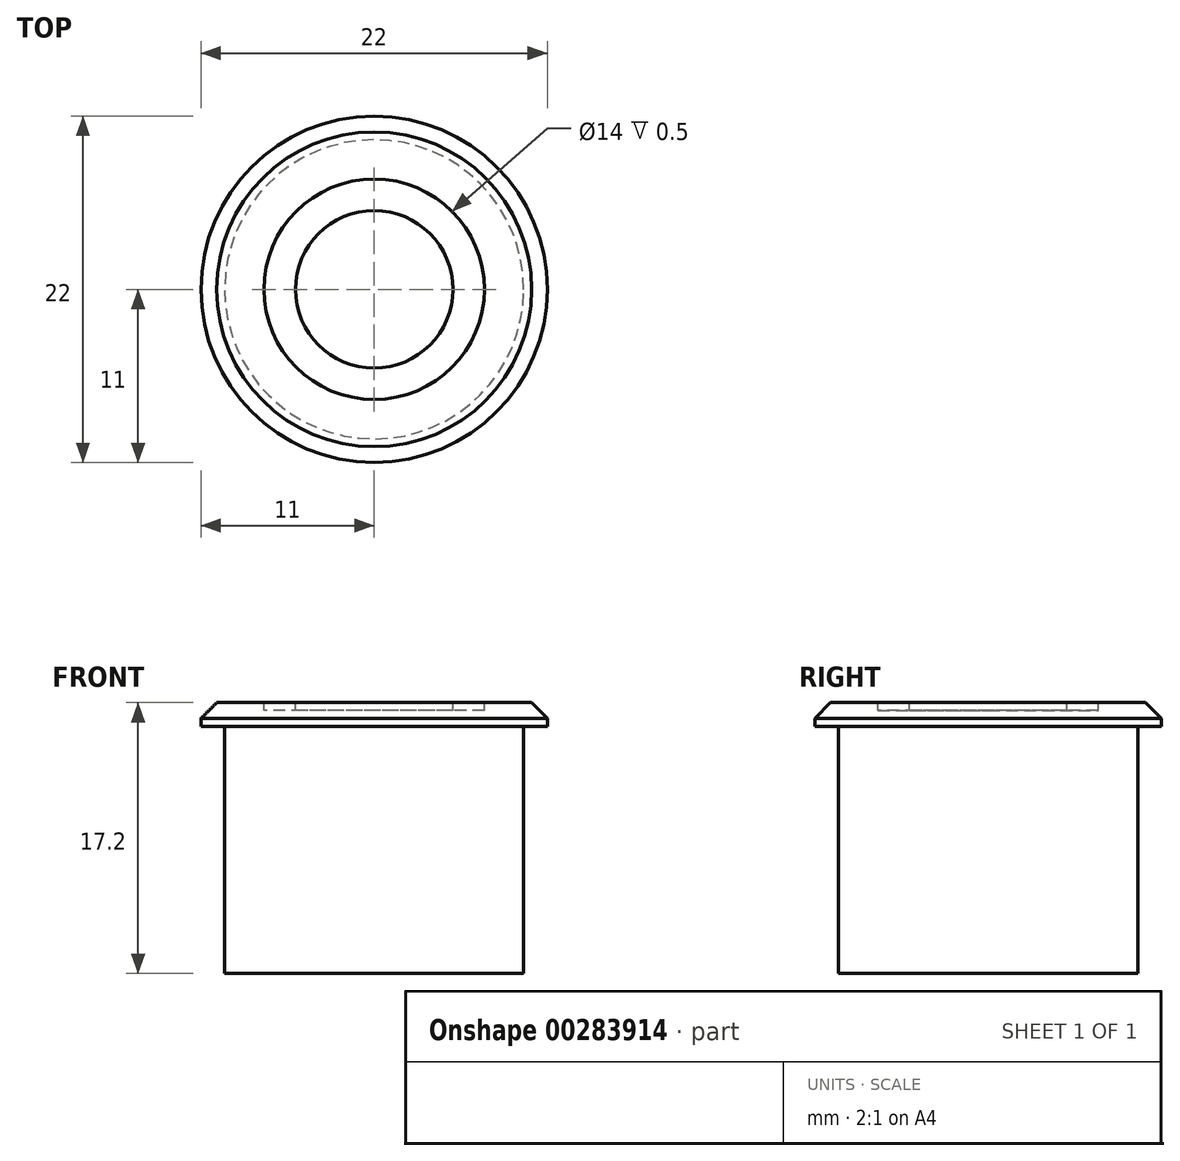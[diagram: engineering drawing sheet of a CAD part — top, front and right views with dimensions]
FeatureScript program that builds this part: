
annotation { "Feature Type Name" : "Feature", "Feature Type Description" : "" }
export const myFeature = defineFeature(function(context is Context, id is Id, definition is map)
    precondition{}
    {
        {
            var Q0;
            Q0=qCreatedBy(makeId("Right.planeOp"),FACE);
            var sketch = newSketch(context, id + "F0", { "sketchPlane" : qUnion([Q0])});
            skLineSegment(sketch, "E0", {"start": v(0, 0) * mm, "end": v(0, 17.2) * mm});
            skLineSegment(sketch, "E1", {"start": v(0, 17.2) * mm, "end": v(10, 17.2) * mm});
            skLineSegment(sketch, "E2", {"start": v(10, 17.2) * mm, "end": v(11, 16.2) * mm});
            skLineSegment(sketch, "E3", {"start": v(11, 16.2) * mm, "end": v(11, 15.7) * mm});
            skLineSegment(sketch, "E4", {"start": v(11, 15.7) * mm, "end": v(9.5, 15.7) * mm});
            skLineSegment(sketch, "E5", {"start": v(9.5, 15.7) * mm, "end": v(9.5, 0) * mm});
            skLineSegment(sketch, "E6", {"start": v(9.5, 0) * mm, "end": v(0, 0) * mm});
            skSolve(sketch);
        }
        {
            var Q0;
            Q0 = qSketchRegion(id + "F0", true);
            var Q1;
            Q1 = qConstructionFilter(qBodyType(qCreatedBy(id + "F0" ,EDGE), BodyType.WIRE), ConstructionObject.NO);
            var Q2;
            Q2=sQuery(id+"F0.wireOp",EDGE,"E0");
            revolve(context, id + "F1", {"entities" : qUnion([Q0]), "surfaceEntities" : qUnion([Q1]), "axis" : qUnion([Q2]), "revolveType" : RevolveType.FULL});
        }
        {
            var Q0;
            Q0=makeQuery(id+"F1.opRevolve","SWEPT_FACE",FACE,{"disambiguationData":[OSD([sQuery(id+"F0.wireOp",EDGE,"E1")])]});
            var sketch = newSketch(context, id + "F2", { "sketchPlane" : qUnion([Q0])});
            skCircle(sketch, "E7", {"center": v(0, 0) * mm, "radius": 7 * mm});
            skCircle(sketch, "E8", {"center": v(0, 0) * mm, "radius": 5 * mm});
            skSolve(sketch);
        }
        {
            var Q0;
            Q0 = qSketchRegion(id + "F2", true);
            extrude(context, id + "F3", {"entities" : qUnion([Q0]), "operationType" : NewBodyOperationType.REMOVE, "oppositeDirection" : true, "depth" : 0.5 * mm});
        }
    });
